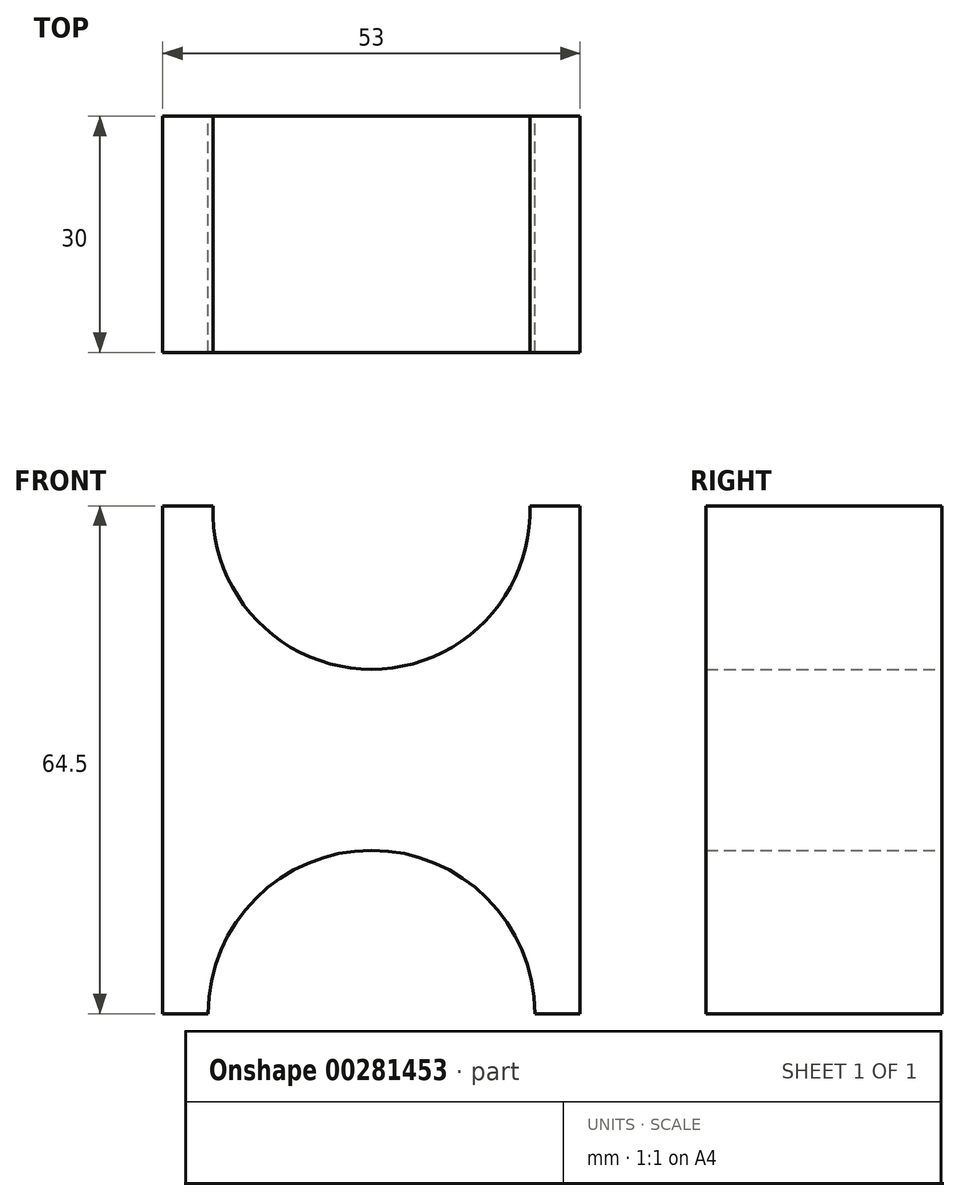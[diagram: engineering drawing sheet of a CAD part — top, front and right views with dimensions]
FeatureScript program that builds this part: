
annotation { "Feature Type Name" : "Feature", "Feature Type Description" : "" }
export const myFeature = defineFeature(function(context is Context, id is Id, definition is map)
    precondition{}
    {
        {
            var Q0;
            Q0=qCreatedBy(makeId("Front.planeOp"),FACE);
            var sketch = newSketch(context, id + "F0", { "sketchPlane" : qUnion([Q0])});
            skLineSegment(sketch, "E0", {"start": v(0, 43.75) * mm, "end": v(0, 20.75) * mm, "construction": true});
            skLineSegment(sketch, "E1", {"start": v(20.14, 64.5) * mm, "end": v(26.5, 64.5) * mm});
            skLineSegment(sketch, "E2", {"start": v(26.5, 64.5) * mm, "end": v(26.5, 0) * mm});
            skLineSegment(sketch, "E3", {"start": v(26.5, 0) * mm, "end": v(20.75, 0) * mm});
            skArc(sketch, "E4", {"start": v(20.75, 0) * mm, "mid": v(14.67, 14.67) * mm, "end": v(0, 20.75) * mm});
            skLineSegment(sketch, "E5.MirrorCS", {"start": v(-26.5, 64.5) * mm, "end": v(-26.5, 0) * mm});
            skLineSegment(sketch, "E6.MirrorCS", {"start": v(-20.14, 64.5) * mm, "end": v(-26.5, 64.5) * mm});
            skLineSegment(sketch, "E7.MirrorCS", {"start": v(-26.5, 0) * mm, "end": v(-20.75, 0) * mm});
            skPoint(sketch, "E8.MirrorCS.start.orphan", {"position": v(0, 43.75) * mm});
            skPoint(sketch, "E9.MirrorCS.end.orphan", {"position": v(0, 20.75) * mm});
            skArc(sketch, "E10", {"start": v(0, 20.75) * mm, "mid": v(-14.67, 14.67) * mm, "end": v(-20.75, 0) * mm});
            skArc(sketch, "E11", {"start": v(-20.14, 64.5) * mm, "mid": v(0, 43.75) * mm, "end": v(20.14, 64.5) * mm});
            skLineSegment(sketch, "E12", {"start": v(-26.5, 32.25) * mm, "end": v(26.5, 32.25) * mm, "construction": true});
            skPoint(sketch, "E13", {"position": v(0, 32.25) * mm});
            skSolve(sketch);
        }
        {
            var Q0;
            Q0=makeQuery(id+"F0.imprint","IMPRINT",FACE,{"disambiguationData":[TD([[makeQuery(id+"F0.imprint","IMPRINT",EDGE,{"derivedFrom":sQuery(id+"F0.wireOp",EDGE,"E1")}),-1.0]])]});
            extrude(context, id + "F1", {"entities" : qUnion([Q0]), "depth" : 30 * mm});
        }
    });
